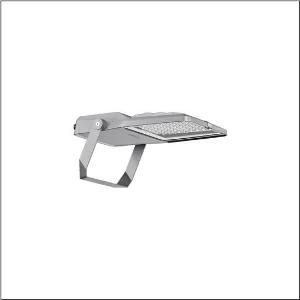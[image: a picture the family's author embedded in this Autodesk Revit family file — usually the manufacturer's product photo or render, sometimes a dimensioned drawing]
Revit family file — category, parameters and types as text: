
# Revit family: floodlight_fl_21_iq_mini___pl64_5xa7772c3e1a_c8ef
name_source: partatom
category: Lighting Fixtures
units: mm (PartAtom-declared; Revit-internal decimal feet)

## family parameters
Cut with Voids When Loaded = No
Host = Face
Light Source = No
Part Type = Normal
Room Calculation Point = No
Round Connector Dimension = Use Diameter
Shared = No

## types (1)
- --- (1 x LED, 10150 lm, 87.2 W, 3000K)
    Apparent Load = 87 VA
    CIE Flux Codes = 28 80 98 100 100
    Color Rendering = 80
    Color Temperature = 3000K
    Default Elevation = 1800 mm
    Description = Floodlight FL 21 iQ mini, floodlight, primary light control with lens, of PMMA, primary optical cover: protective disc, of toughened safety glass, transparent, light distribution: PL64, light emission: direct distribution, installation type: surface-mounted, LED, High Power LED, rated luminous flux: 10.150lm, luminous efficacy: 116lm/W, light colour: 830, colour temperature: 3000K, control: Street-Remote, Auto-Match, Temp-Guard, Night-Set, Smart-Wire, Desk-Remote (wireless, voltage-free reading and setting of iQ features in the workshop via application-optimized NFC function/RFID function), optimised constant luminous flux control (CLO 2.0), with terminal, 6-pole, mains connection: 220..240V, AC, 50/60Hz, start of lifetime: 87W, end of service life: 92W, reduction: 40W, luminaire housing, of diecast aluminium, powder-coated, Siteco® metallic grey (DB 702S), corrosivity category C5 mid according to DIN EN ISO 12944, sealing non-destructively replaceable, mounting bracket, of steel, galvanised, powder-coated, Siteco® metallic grey (DB 702S), protection rating (complete): IP66, insulation class (complete): insulation class II (safety insulation), certification: CE, ENEC, VDE, protection symbol: D, impact resistance: IK08, permissible operating ambient temperature: -40..+40°C, permissible operating ambient temperature for outdoor applications: -40..+50°C, standard: DIN EN 12944, LABS conformity tested according to VDMA 24364:2018-05, packaging unit: 1 piece

Light Distribution: PL64
    Height = 70 mm
    Lamp = 1 x LED
    Lamp Light Flux = 10150 lm
    Lamp Power = 87.2 W
    Lamp count = 1
    Length = 485 mm
    Luminous efficacy = 116 lm/W
    Manufacturer = Siteco
    ModVariant = No
    Model = 5XA7772C3E1A
    Number of Poles = 1
    OnlyDefault = Yes
    Power Factor = 1
    Product Name = Floodlight FL 21 iQ mini | PL64
    Product group = floodlight | pylon annexe
    ProductGroupID = 6200
    Protection Class = Protection class II
    Protection Degree = IP 66
    RLX_Detail_Level = 1
    RLX_Emergency_Light_Flux = 0 lm
    RLX_Emergency_Type = 0
    RLX_Emergency_Type_DB = No
    RlxData = <blob elided: 96229 chars, md5=d371d10a>
    Socket = socket
    Standby Power = 0 W
    System Light Flux = 10150 lm
    System Power = 87 W
    Type Comments = factory setting: luminous flux: 100 % | dim-lin: 254 | 456 mA
    Type Image = l_1006845.jpg
    URL = http://relux.com
    VarID = @adj_116477
    Voltage = 0 V
    Weight = 0.00 kg
    Width = 337 mm

## geometry (parser evidence)
native form markers: Blend x4, Sweep x14
no freeform markers — native parametric forms only
